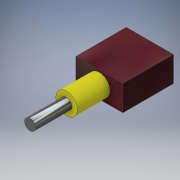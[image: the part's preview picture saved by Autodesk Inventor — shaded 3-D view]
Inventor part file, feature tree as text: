
AUTODESK INVENTOR PART (.ipt)
format: ipt  version: 2016 (Build 200138000, 138)  size: 133,120 bytes
history: native  units: in
note: dims shown in document units (in); Inventor stores cm internally (conversion verified against a paired STEP export)
features: extrude x3, sketch x3
ambient origin geometry x8: Origin, YZ Plane, XZ Plane, XY Plane, X Axis, Y Axis, Z Axis, Center Point
bodies: Solid1 (feature_tree)
feature tree (6):
  extrude  "Extrusion1"  Depth=0.27in
  extrude  "Extrusion2"  Depth=0.541in
  extrude  "Extrusion3"  Depth=0.39in
  sketch  "Sketch1"  dims[d0=0.504in d1=0.27in]
  sketch  "Sketch2"  dims[d2=0.541in d3=0.0in d4=0.23in]
  sketch  "Sketch3"  dims[d5=0.252in d6=0.135in d7=0.35in d8=0.0in d9=0.118in d10=0.39in d11=0.0in]
